# Revit family: ADB Fourneaux Gaz  Gastro L1000 2
name_source: partatom
category: Equipement spécialisé
units: mm (PartAtom-declared; Revit-internal decimal feet)

## family parameters
Basée sur le plan de construction = Non
Conserver l'orientation des annotations = Non
Cote de connecteur circulaire = Utiliser le diamètre
Couper avec des vides une fois chargée = Non
Numéro OmniClass = 23.40.40.14.17.11
Partagée = Non
Repère de localisation dans la pièce = Non
Titre OmniClass = Cookers, Ovens, Stoves
Toujours verticalement = Oui
Type d'élément = Normal

## types (3) — shared parameters
Commentaires du type = Gamme Ambassade - Fourneaux gaz
Diamètre de Raccordement Gaz = 21 mm
Fabricant = Société Industrielle de Lacanche
Pbase = 0 W
Pbase gaz = 26 W
URL = https://www.ambassade-de-bourgogne.com
zero-valued in all types: Elévation par défaut

## per-type parameters (varying)
| type | Bouton hors CG 1041 GAGCF | Description | Modèle | Plaques | Poids net à vide |
| 4 feux vifs - 1 plaque coup de feu - 1 four - CG 1051 GACF | Oui | Fourneau 4 feux vifs - 1 plaque coup de feu - 1 four gaz Gastronome 1/1 | CG 1051 GAGCF | CG1052GA_CG1051GACF_CG1041GAGCF_Fourneaux 5-4-2 feux vifs : CG 1051 GACF | 126.00 kg |
| 2 feux vifs - 1 plaque coup de feu - 1 four - CG 1041 GAGCF | Non | Fourneau 2 feux vifs - 1 plaque coup de feu 650 x 500 - 1 four gaz Gastronome 1/1 | CG 1041 GAGCF | CG1052GA_CG1051GACF_CG1041GAGCF_Fourneaux 5-4-2 feux vifs : CG 1041 GAGCF | 125.00 kg |
| 5 feux vifs - 1 four - CG 1051 GA | Oui | Fourneau 5 feux vifs - 1 four gaz Gastronome 1/1 | CG 1051 GA | CG1052GA_CG1051GACF_CG1041GAGCF_Fourneaux 5-4-2 feux vifs : CG 1051 GA | 114.00 kg |
